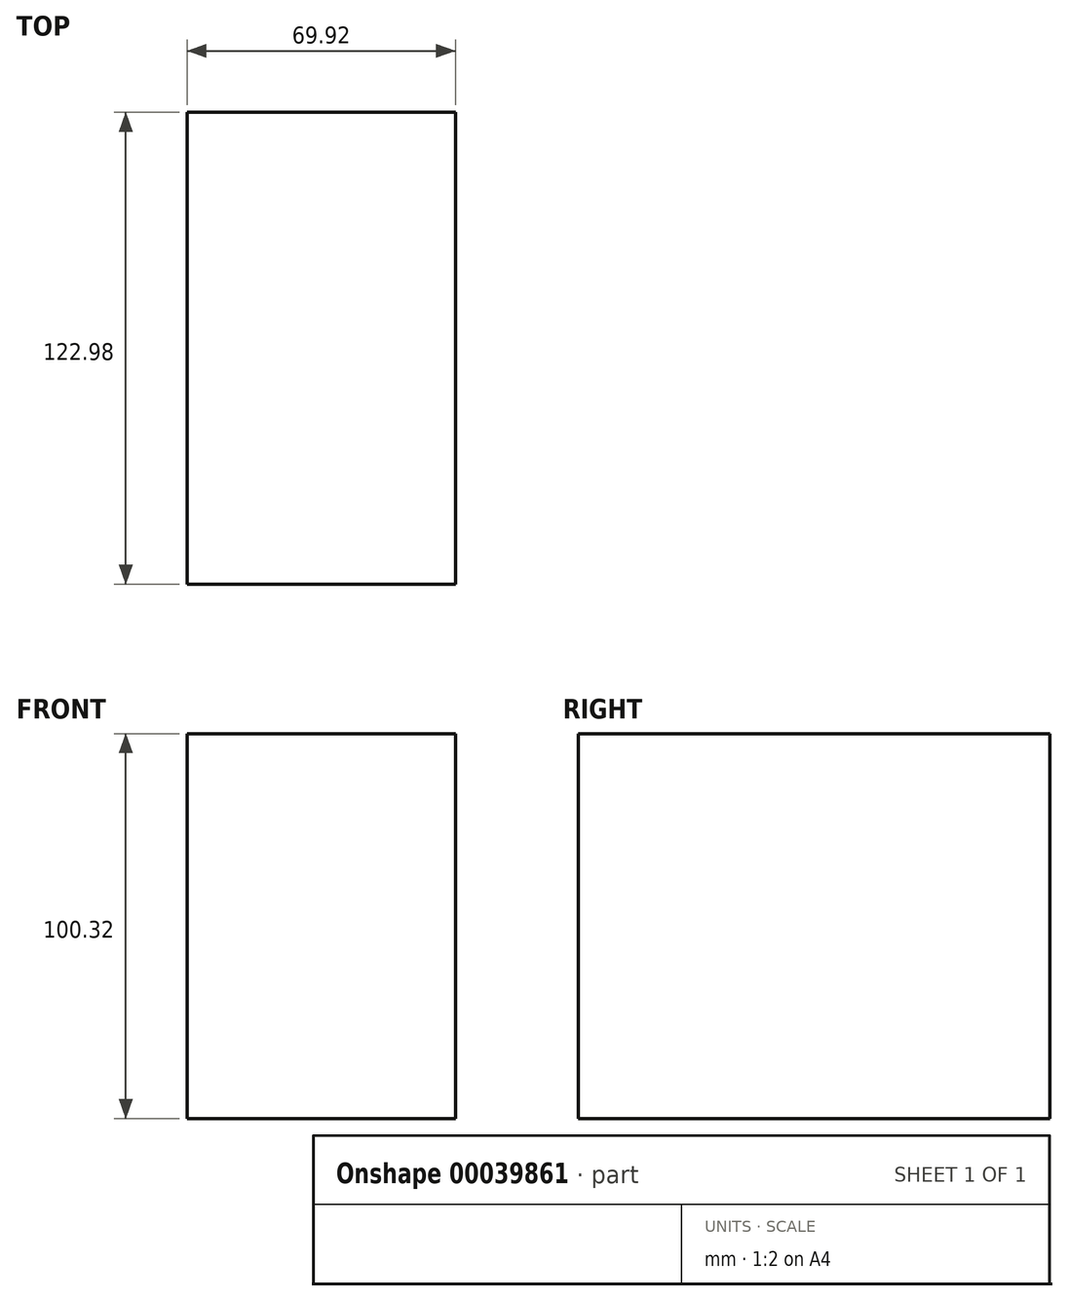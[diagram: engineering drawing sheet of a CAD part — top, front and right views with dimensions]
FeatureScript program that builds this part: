
annotation { "Feature Type Name" : "Feature", "Feature Type Description" : "" }
export const myFeature = defineFeature(function(context is Context, id is Id, definition is map)
    precondition{}
    {
        {
            var Q0;
            Q0=qCreatedBy(makeId("Right.planeOp"),FACE);
            var sketch = newSketch(context, id + "F0", { "sketchPlane" : qUnion([Q0])});
            skLineSegment(sketch, "E0.bottom", {"start": v(0, 0) * mm, "end": v(122.98, 0) * mm});
            skLineSegment(sketch, "E0.top", {"start": v(0, -100.32) * mm, "end": v(122.98, -100.32) * mm});
            skLineSegment(sketch, "E0.left", {"start": v(0, 0) * mm, "end": v(0, -100.32) * mm});
            skLineSegment(sketch, "E0.right", {"start": v(122.98, 0) * mm, "end": v(122.98, -100.32) * mm});
            skSolve(sketch);
        }
        {
            var Q0;
            Q0 = qSketchRegion(id + "F0", true);
            extrude(context, id + "F1", {"entities" : qUnion([Q0]), "oppositeDirection" : true, "depth" : 69.92 * mm});
        }
    });
